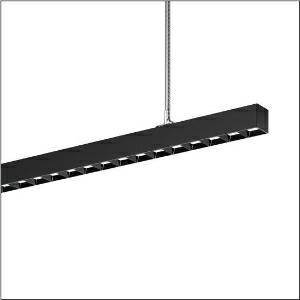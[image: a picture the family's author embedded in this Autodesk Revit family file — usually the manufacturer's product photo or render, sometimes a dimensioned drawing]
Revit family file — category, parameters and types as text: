
# Revit family: silica_r__21_51mx31dc3dbb_16a7
name_source: partatom
category: Lighting Fixtures
units: mm (PartAtom-declared; Revit-internal decimal feet)

## family parameters
Cut with Voids When Loaded = No
Host = Face
Light Source = No
Part Type = Normal
Room Calculation Point = No
Round Connector Dimension = Use Diameter
Shared = No

## types (1)
- --- (1 x LED, 18230 lm, 113.3 W, 3000K)
    Apparent Load = 113 VA
    CIE Flux Codes = 87 99 100 59 100
    Color Rendering = 80
    Color Temperature = 3000K
    Default Elevation = 1800 mm
    Description = Silica® 21, office luminaire, primary light control with darklight reflector, of PMMA, black, CAT 2 (L<= 3000cd/m²), light emission: direct/indirect distribution, primary light characteristic: symmetric, installation type: suspended mounting, LED, rated luminous flux: 18.230lm, luminous efficacy: 161lm/W, light colour: 830, colour temperature: 3000K, control gear: DALI 2, with terminal, 3+2-pole, max. 2.5mm², mains connection: 220..240V, AC, 50/60Hz, rated input power: 113.3W, luminaire housing, of aluminium, matt jet black (RAL 9005), length: 3.004mm, width: 53mm, height: 53mm, protection rating (complete): IP20, insulation class (complete): insulation class I (protective earthing), certification: CE, permissible operating ambient temperature: 0..+35°C, standard: EN 50419, packaging unit: 1 piece
    Height = 53 mm
    Lamp = 1 x LED
    Lamp Light Flux = 18230 lm
    Lamp Power = 113.3 W
    Lamp count = 1
    Length = 3004 mm
    Luminous efficacy = 161 lm/W
    Manufacturer = Siteco
    ModVariant = No
    Model = 51MX31DC3DBB
    Mounting Place = Ceiling
    Mounting Type = Pendant
    Number of Poles = 1
    OnlyDefault = Yes
    Power Factor = 1
    Product Name = Silica® 21
    Product group = office luminaire | ceiling pendant
    ProductGroupID = 903
    Protection Class = Protection class I
    Protection Degree = IP 20
    RLX_Detail_Level = 1
    RLX_Emergency_Light_Flux = 0 lm
    RLX_Emergency_Type = 0
    RLX_Emergency_Type_DB = No
    RlxData = <blob elided: 66501 chars, md5=9a332744>
    Socket = socket
    Standby Power = 0 W
    System Light Flux = 18230 lm
    System Power = 113 W
    Type Comments = factory setting: luminous flux: 100 % | dim-lin: 254 | 392 mA
    Type Image = l_1335852.jpg
    URL = http://relux.com
    VarID = @adj_142581
    Voltage = 0 V
    Weight = 0.00 kg
    Width = 53 mm

## geometry (parser evidence)
native form markers: Blend x4, Sweep x11
no freeform markers — native parametric forms only
